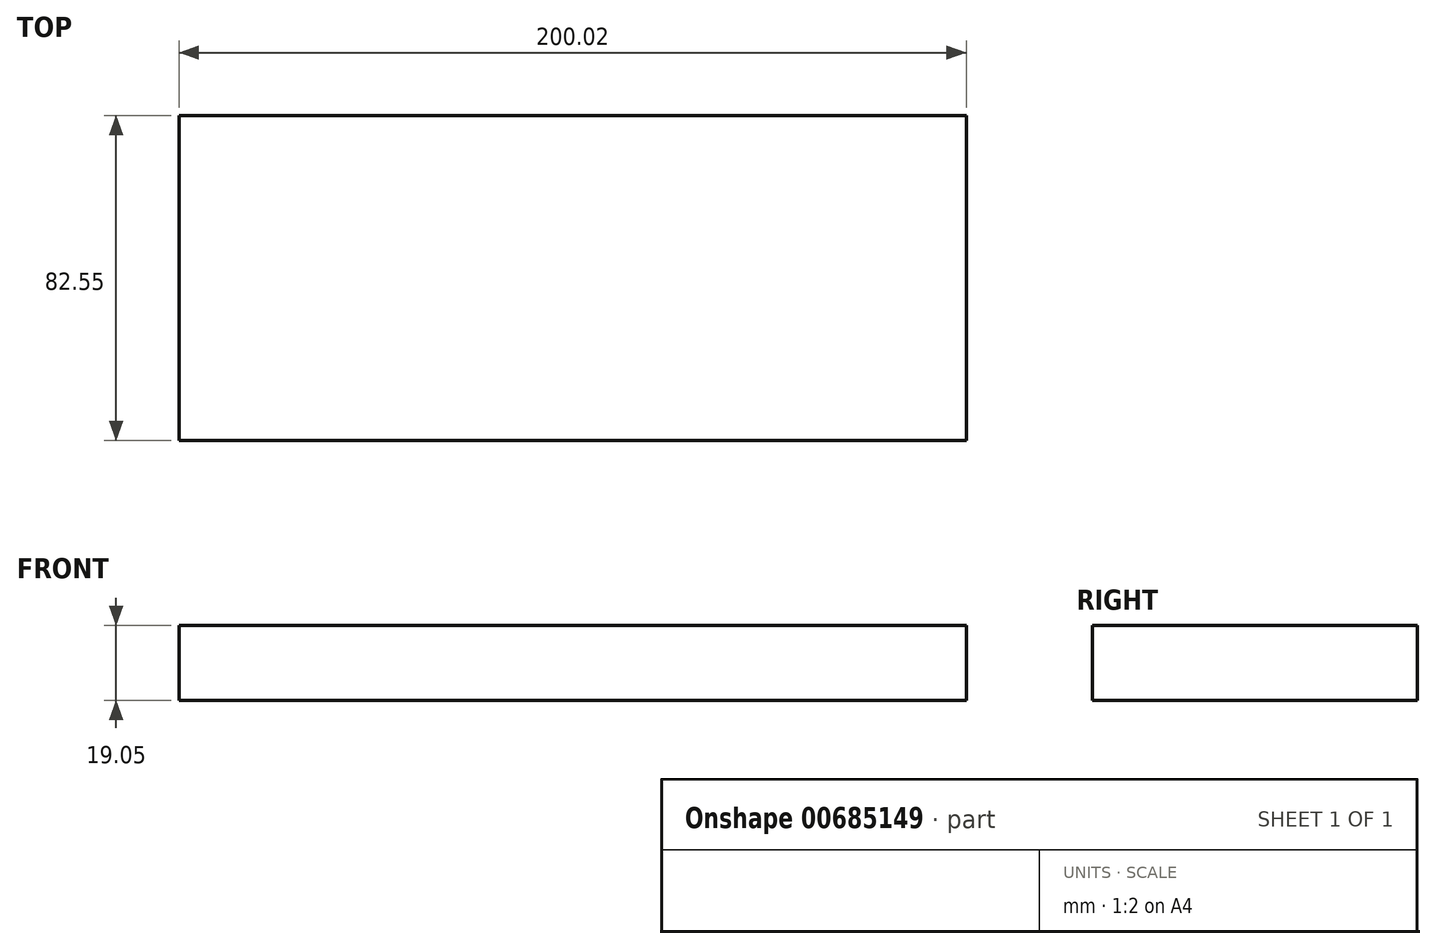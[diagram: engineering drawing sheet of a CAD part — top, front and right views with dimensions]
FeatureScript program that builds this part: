
annotation { "Feature Type Name" : "Feature", "Feature Type Description" : "" }
export const myFeature = defineFeature(function(context is Context, id is Id, definition is map)
    precondition{}
    {
        {
            var Q0;
            Q0=qCreatedBy(makeId("Top.planeOp"),FACE);
            var sketch = newSketch(context, id + "F0", { "sketchPlane" : qUnion([Q0])});
            skLineSegment(sketch, "E0.bottom", {"start": v(-75.17, 0) * mm, "end": v(124.85, 0) * mm});
            skLineSegment(sketch, "E0.top", {"start": v(-75.17, -82.55) * mm, "end": v(124.85, -82.55) * mm});
            skLineSegment(sketch, "E0.left", {"start": v(-75.17, 0) * mm, "end": v(-75.17, -82.55) * mm});
            skLineSegment(sketch, "E0.right", {"start": v(124.85, 0) * mm, "end": v(124.85, -82.55) * mm});
            skSolve(sketch);
        }
        {
            var Q0;
            Q0 = qSketchRegion(id + "F0", true);
            extrude(context, id + "F1", {"entities" : qUnion([Q0]), "depth" : 19.05 * mm, "offsetDistance" : 25.4 * mm});
        }
    });
